# Revit family: Isolation_Pump-Flanges-WATTS-IPF_Series
name_source: partatom
category: Pipe Accessories
revit_build: Autodesk Revit 2014 (Build: 20130308_1515(x64)
units: mm (PartAtom-declared; Revit-internal decimal feet)

## types (13) — shared parameters
Assembly Code = D2090900
CW Connection = Yes
Country = United States
Description = Series IPF Isolation Pump Flanges for Circulator Pumps Sizes: 3⁄4" – 2" Series IPF Isolation Pump Flanges are designed to isolate circulator pumps to facilitate circulator pump replacement or repair.
Height = 2 11/16"
Manufacturer = WATTS
Manufacturer Product Line = Water Safety & Flow Control
Materials = Metal-WATTS-Brass
Max. Working Pressure = Maximum Working Pressure: 400psi (28 bar) WOG
Maximum Temperature = 406°F (208°C) @ 100psi (6.9 bar)
Price = Prices may vary. Please consult Manufacturer Representative for most up-to-date price list.
Product Documentation Link = https://www.watts.com
Product Page URL = https://www.watts.com
Region = North America
URL = http://www.watts.com
Warranty Information = 1 Year (Limited)

## per-type parameters (varying)
| type | Cold Water Connection Diameter | Cold Water Connection Radius | Connection Inlet Description | Connection Outlet Description | Connection Type | Handle Length C | Length | Nominal Width D | Width | lenght /2 |
| IPF-T-M1 3/4" | 3/4" | 3/8" | 3/4" Flanged Connection | 3/4" NPT Threaded End Connection | Flanged Connection X  NPT Threaded | 3" | 2 1/2" | 3 3/16" | 4 5/8" | 1 1/4" |
| IPF-T-M1 1" | 1" | 1/2" | 1" Flanged Connection | 1" NPT Threaded End Connection | Flanged Connection X NPT Threaded | 3" | 2 5/8" | 3 3/16" | 4 5/8" | 1 5/16" |
| IPF-T-M1 1 1/4" | 1 1/4" | 5/8" | 1 1/4" Flanged Connection | 1 1/4" NPT Threaded End Connection | Flanged Connection X NPT Threaded | 4" | 2 13/16" | 3 3/16" | 4 5/8" | 1 13/32" |
| IPF-T-M1 1 1/2" | 1 1/2" | 3/4" | 1 1/2" Flanged Connection | 1 1/2" NPT Threaded End Connection | Flanged Connection X NPT Threaded | 4" | 3 1/4" | 3 3/16" | 4 5/8" | 1 5/8" |
| IPF-T-M1 2" | 2" | 1" | 2"  Flanged Connection | 2" NPT Threaded End Connection | Flanged Connection X NPT Threaded | 4" | 3 3/4" | 3 7/16" | 4 5/8" | 1 7/8" |
| IPF-S-M1 3/4" | 3/4" | 3/8" | 3/4" Flanged Connection | 3/4" Solder end Connection | Flanged Connection X Solder end | 3" | 3 1/8" | 3 3/16" | 4 5/8" | 1 9/16" |
| IPF-S-M1 1" | 1" | 1/2" | 1" Flanged Connection | 1" Solder end Connection | Flanged Connection X Solder end | 3" | 3 1/2" | 3 3/16" | 4 5/8" | 1 3/4" |
| IPF-S-M1 1 1/4" | 1 1/4" | 5/8" | 1 1/4" Flanged Connection | 1 1/4" Solder end Connection | Flanged Connection X Solder end | 4" | 2 13/16" | 3 3/16" | 4 5/8" | 1 13/32" |
| IPF-S-M1 1 1/2" | 1 1/2" | 3/4" | 1 1/2" Flanged Connection | 1 1/2" Solder end Connection | Flanged Connection X Solder end | 4" | 3 1/8" | 3 3/16" | 4 5/8" | 1 9/16" |
| IPF-S-M1 2" | 2" | 1" | 2" Flanged Connection | 2" Solder end Connection | Flanged Connection X Solder end | 4" | 3 1/2" | 3 7/16" | 4 5/8" | 1 3/4" |
| IPF-PRESS-M1 3/4" | 3/4" | 3/8" | 3/4" Flanged Connection | 3/4" Press end Connection | Flanged Connection X Press end | 3 5/8" | 3" | 3 3/16" | 4 1/8" | 1 1/2" |
| IPF-PRESS-M1 1" | 1" | 1/2" | 1" Flanged Connection | 1" Press end Connection | Flanged Connection X Press end | 4" | 3 5/16" | 3 3/16" | 4 1/8" | 1 21/32" |
| IPF-PRESS-M1 1 1/4" | 1 1/4" | 5/8" | 1 1/4" Flanged Connection | 1 1/4" Press end Connection | Flanged Connection X Press end | 5 7/16" | 3 5/8" | 3 3/16" | 4 1/8" | 1 13/16" |

note: column(s) folded — value = type name in every type: Model

## geometry (parser evidence)
native form markers: Sweep x1
no freeform markers — native parametric forms only
